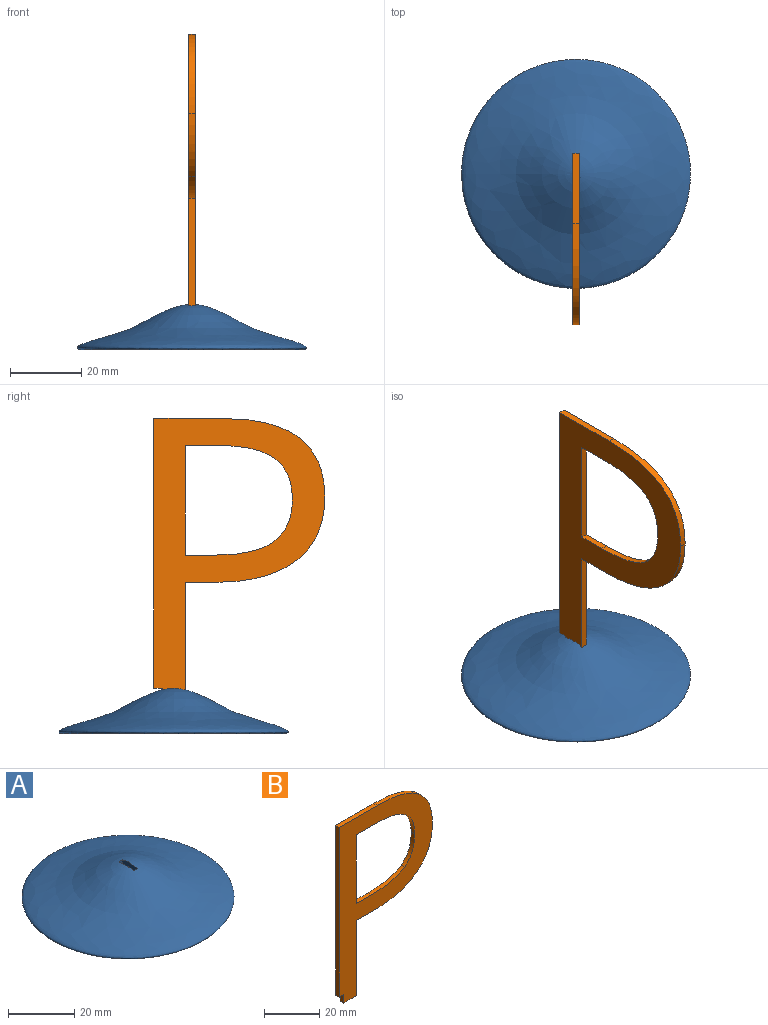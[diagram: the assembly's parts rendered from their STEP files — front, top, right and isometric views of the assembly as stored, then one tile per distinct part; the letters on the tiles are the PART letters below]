
ASSEMBLY  parts=2 mates=1
PART A: 7 faces, bbox 64.4x64.4x12.9 mm
  f0: revolved ~64.13x64.13mm, area 3625.5mm2, adj f2,f3,f4,f5,f6
  f1: revolved ~59.4x59.4mm, area 2948mm2, adj f2,f3,f4,f5,f6
  f2: plane 63.5x63.5mm, normal (0,0,-1), area 395.5mm2, adj f0,f1
  f3: plane 6.6x2.28mm, normal (1,0,0), area 11.9mm2, adj f0,f1,f4,f6
  f4: plane 2.11x2.02mm, normal (0,1,0), area 3.3mm2, adj f0,f1,f3,f5
  f5: plane 6.6x2.28mm, normal (-1,0,0), area 11.9mm2, adj f0,f1,f4,f6
  f6: plane 2.11x2.02mm, normal (0,-1,0), area 3.3mm2, adj f0,f1,f3,f5
PART B: 19 faces, bbox 47.9x1.8x79.4 mm
  f0: plane 7.92x1.78mm, normal (0,0,1), area 14.1mm2, adj f1,f14,f15,f16
  f1: plane 30.69x1.78mm, normal (1,0,0), area 54.6mm2, adj f0,f2,f15,f16
  f2: plane 9.82x1.78mm, normal (0,0,-1), area 17.5mm2, adj f1,f3,f15,f16
  f3: extruded ~15.3x3.66mm, area 28.4mm2, adj f2,f4,f15,f16
  f4: extruded ~11.15x4.91mm, area 22.5mm2, adj f3,f5,f15,f16
  f5: extruded ~12.1x5.22mm, area 24.4mm2, adj f4,f14,f15,f16
  f6: extruded ~17.65x7.83mm, area 35.6mm2, adj f7,f13,f15,f16
  f7: extruded ~28.31x22.01mm, area 72.8mm2, adj f6,f8,f15,f16
  f8: plane 19.6x1.78mm, normal (0,0,1), area 34.8mm2, adj f7,f9,f15,f16
  f9: plane 75.56x1.78mm, normal (-1,0,0), area 134.3mm2, adj f8,f10,f15,f16
  f10: plane 2.36x1.78mm, normal (0,0,-1), area 4.2mm2, adj f9,f15,f16,f17
  f11: plane 33.53x1.78mm, normal (1,0,0), area 59.6mm2, adj f12,f15,f16,f18
  f12: plane 8.9x1.78mm, normal (0,0,-1), area 15.8mm2, adj f11,f13,f15,f16
  f13: extruded ~22.4x6.18mm, area 42.1mm2, adj f6,f12,f15,f16
  f14: extruded ~16.89x3.77mm, area 31.2mm2, adj f0,f5,f15,f16
  f15: plane 79.37x47.91mm, normal (0,-1,0), area 1431.5mm2, adj f0,f1,f2,f3,f4,f5,f6,f7
  f16: plane 79.37x47.91mm, normal (0,1,0), area 1431.5mm2, adj f0,f1,f2,f3,f4,f5,f6,f7
  f17: plane 3.81x1.78mm, normal (-1,0,0), area 6.8mm2, adj f10,f15,f16,f18
  f18: plane 6.42x1.78mm, normal (0,0,-1), area 11.4mm2, adj f11,f15,f16,f17
PLACE A at identity
PLACE B rot(axis=(0,0,-1),90deg) t=(0.89,15.96,9.68)mm
MATE fastened B.f18 <-> A.f0  axis (0,0,-1) through (0,0,8.88)mm
